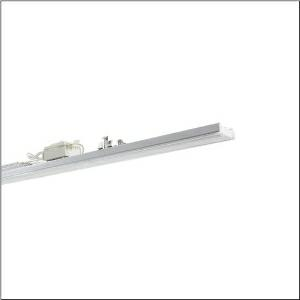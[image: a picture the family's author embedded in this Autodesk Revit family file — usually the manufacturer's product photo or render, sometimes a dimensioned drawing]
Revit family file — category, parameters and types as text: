
# Revit family: licross_r__21_recessed_ho_52tl12dn5e5m_1cf5
name_source: partatom
category: Lighting Fixtures
units: mm (PartAtom-declared; Revit-internal decimal feet)

## family parameters
Cut with Voids When Loaded = No
Host = Face
Light Source = No
Part Type = Normal
Room Calculation Point = No
Round Connector Dimension = Use Diameter
Shared = No

## types (1)
- --- (1 x LED, 14860 lm, 84.6 W, 5000K)
    Apparent Load = 85 VA
    CIE Flux Codes = 69 91 98 100 100
    Color Rendering = 80
    Color Temperature = 5000K
    Default Elevation = 1800 mm
    Description = Licross® 21 Recessed HO, luminaire insert, of sheet steel, galvanised, coil coated, white, length: 1.500mm, width: 66mm, height: 67mm, LED rated luminous flux: 14.860lm, light colour: 850, control gear: DALI 2, with plug, 5-pole, with phase selection, mains connection: 220..240V, AC, 50/60Hz, rated input power: 85W, internal wiring halogen-free, primary optical cover: cover, of PMMA, light emission: direct distribution, primary light characteristic: symmetric, protection rating (complete): IP40, insulation class (complete): insulation class I (protective earthing), certification: CE, ENEC, VDE, UKCA, protection symbol: D if used in an environment without relevant dust loads with corresponding accessories, impact resistance: IK06, permissible ambient temperature for indoor applications: -25..+30°C, corresponds to IFS (International Featured Standards) requirements for safety and quality in the food industry, reducing of maximum allowable ambient temperature of 5°C with ceiling mounting, LABS conformity tested according to VDMA 24364:2018-05, packaging unit: 1 piece
    Height = 58 mm
    Lamp = 1 x LED
    Lamp Light Flux = 14860 lm
    Lamp Power = 84.6 W
    Lamp count = 1
    Length = 1500 mm
    Luminous efficacy = 176 lm/W
    Manufacturer = Siteco
    ModVariant = No
    Model = 52TL12DN5E5M
    Mounting Place = Ceiling
    Mounting Type = Pendant
    Number of Poles = 1
    OnlyDefault = Yes
    Power Factor = 1
    Product Name = Licross® 21 Recessed HO
    Product group = luminaire insert | ceiling pendant
    ProductGroupID = 902
    Protection Class = Protection class I
    Protection Degree = IP 40
    RLX_Detail_Level = 1
    RLX_Emergency_Light_Flux = 0 lm
    RLX_Emergency_Type = 0
    RLX_Emergency_Type_DB = No
    RlxData = <blob elided: 24729 chars, md5=d3783b98>
    Socket = socket
    Standby Power = 0 W
    System Light Flux = 14860 lm
    System Power = 85 W
    Type Comments = factory setting: luminous flux: 100 % | dim-lin: 254 | 484 mA
    Type Image = l_1296930.jpg
    URL = http://relux.com
    VarID = @adj_110533
    Voltage = 0 V
    Weight = 0.00 kg
    Width = 66 mm

## geometry (parser evidence)
native form markers: Blend x4, Sweep x13
no freeform markers — native parametric forms only
